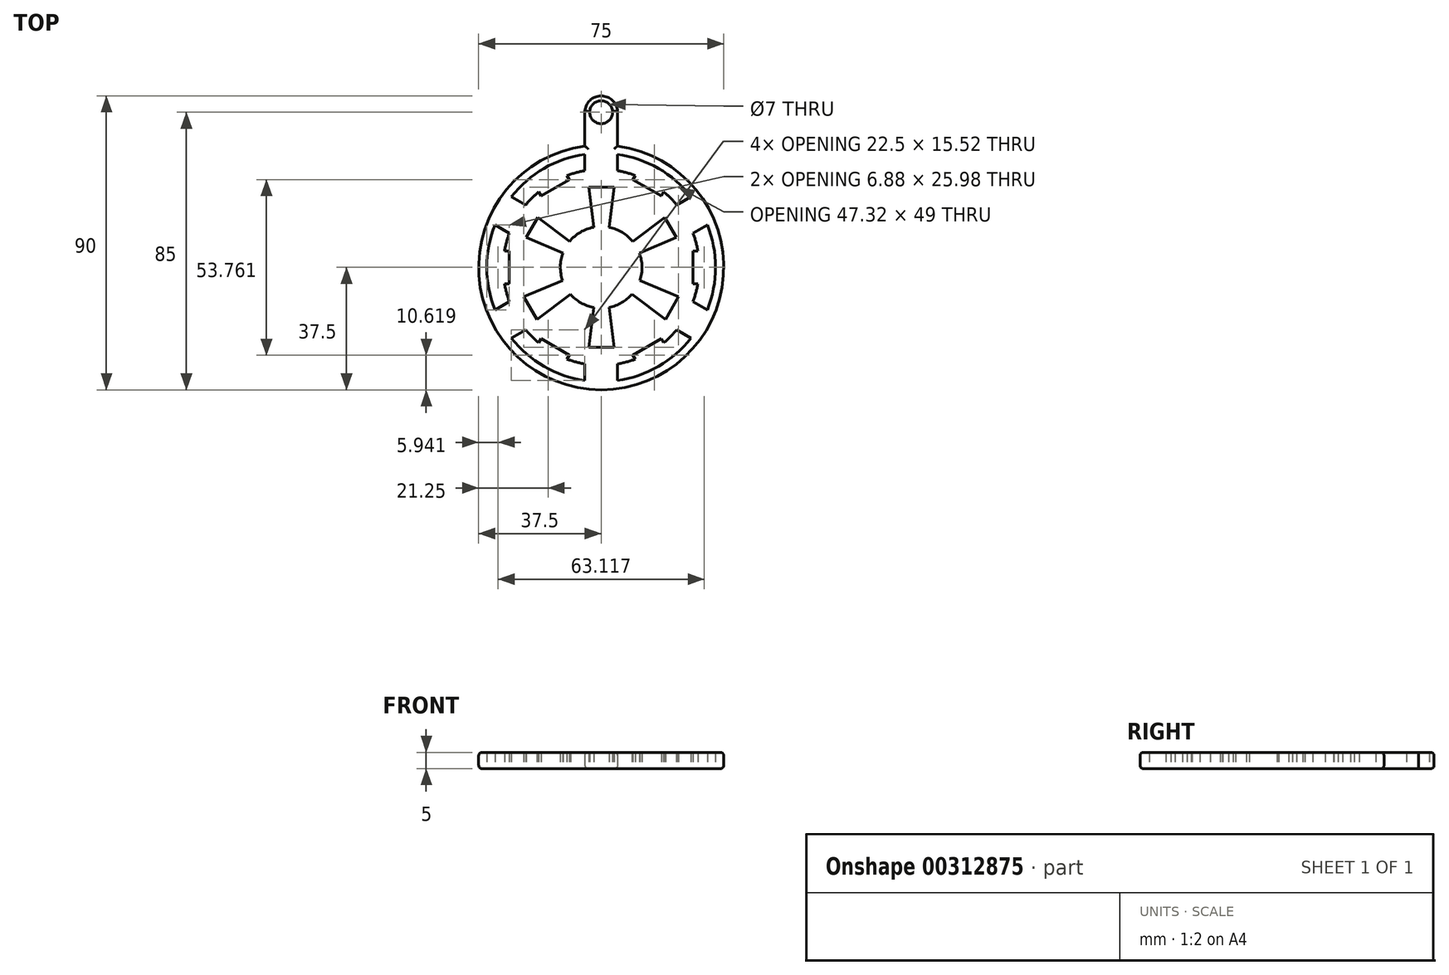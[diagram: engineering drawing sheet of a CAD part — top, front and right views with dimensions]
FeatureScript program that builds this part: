
annotation { "Feature Type Name" : "Feature", "Feature Type Description" : "" }
export const myFeature = defineFeature(function(context is Context, id is Id, definition is map)
    precondition{}
    {
        {
            var Q0;
            Q0=qCreatedBy(makeId("Top.planeOp"),FACE);
            var sketch = newSketch(context, id + "F0", { "sketchPlane" : qUnion([Q0])});
            skArc(sketch, "E0", {"start": v(-5, 29.58) * mm, "mid": v(-7.76, 28.98) * mm, "end": v(-10.46, 28.12) * mm});
            skLineSegment(sketch, "E1", {"start": v(-5, 30) * mm, "end": v(-5, 34.64) * mm});
            skLineSegment(sketch, "E2", {"start": v(5, 30) * mm, "end": v(5, 34.64) * mm});
            skLineSegment(sketch, "E3", {"start": v(-5, 30) * mm, "end": v(-5, 29.58) * mm});
            skLineSegment(sketch, "E4", {"start": v(5, 30) * mm, "end": v(5, 29.58) * mm});
            skLineSegment(sketch, "E5", {"start": v(-5, -30) * mm, "end": v(-5, -34.64) * mm});
            skLineSegment(sketch, "E6", {"start": v(-5, -30) * mm, "end": v(-5, -29.58) * mm});
            skArc(sketch, "E7.trimOffspring", {"start": v(5, -29.58) * mm, "mid": v(7.76, -28.98) * mm, "end": v(10.46, -28.12) * mm});
            skLineSegment(sketch, "E8.MirrorCS", {"start": v(5, -30) * mm, "end": v(5, -29.58) * mm});
            skLineSegment(sketch, "E9.MirrorCS", {"start": v(5, -30) * mm, "end": v(5, -34.64) * mm});
            skLineSegment(sketch, "E10", {"start": v(-27.5, 21.65) * mm, "end": v(-23.12, 19.12) * mm});
            skLineSegment(sketch, "E11", {"start": v(-32.5, 13) * mm, "end": v(-28.12, 10.46) * mm});
            skArc(sketch, "E12.trimOffspring", {"start": v(-28.12, 10.46) * mm, "mid": v(-28.98, 7.76) * mm, "end": v(-29.58, 5) * mm});
            skLineSegment(sketch, "E13", {"start": v(-27.5, -21.65) * mm, "end": v(-23.12, -19.12) * mm});
            skLineSegment(sketch, "E14", {"start": v(-32.5, -13) * mm, "end": v(-28.12, -10.46) * mm});
            skArc(sketch, "E15.trimOffspring", {"start": v(-23.12, -19.12) * mm, "mid": v(-21.21, -21.21) * mm, "end": v(-19.12, -23.12) * mm});
            skLineSegment(sketch, "E16.MirrorCS", {"start": v(27.5, 21.65) * mm, "end": v(23.12, 19.12) * mm});
            skLineSegment(sketch, "E17.MirrorCS", {"start": v(32.5, 13) * mm, "end": v(28.12, 10.46) * mm});
            skLineSegment(sketch, "E18.MirrorCS", {"start": v(32.5, -13) * mm, "end": v(28.12, -10.46) * mm});
            skLineSegment(sketch, "E19.MirrorCS", {"start": v(27.5, -21.65) * mm, "end": v(23.12, -19.12) * mm});
            skArc(sketch, "E20.trimOffspring", {"start": v(23.12, 19.12) * mm, "mid": v(21.21, 21.21) * mm, "end": v(19.12, 23.12) * mm});
            skArc(sketch, "E21.trimOffspring", {"start": v(28.12, -10.46) * mm, "mid": v(28.98, -7.76) * mm, "end": v(29.58, -5) * mm});
            skCircle(sketch, "E22", {"center": v(0, 0) * mm, "radius": 37.5 * mm});
            skLineSegment(sketch, "E23", {"start": v(-18.39, 21.85) * mm, "end": v(-9.73, 26.85) * mm});
            skLineSegment(sketch, "E24", {"start": v(-9.73, 26.85) * mm, "end": v(-10.46, 28.12) * mm});
            skLineSegment(sketch, "E25", {"start": v(-18.39, 21.85) * mm, "end": v(-19.12, 23.12) * mm});
            skArc(sketch, "E26.trimOffspring", {"start": v(-19.12, 23.12) * mm, "mid": v(-21.21, 21.21) * mm, "end": v(-23.12, 19.12) * mm});
            skPoint(sketch, "E27.start.orphan", {"position": v(-14.06, 24.35) * mm});
            skLineSegment(sketch, "E28", {"start": v(-28.12, 5) * mm, "end": v(-28.12, -5) * mm});
            skPoint(sketch, "E29.endSnap0", {"position": v(-28.12, 0) * mm});
            skLineSegment(sketch, "E30", {"start": v(-28.12, 5) * mm, "end": v(-29.58, 5) * mm});
            skLineSegment(sketch, "E31", {"start": v(-28.12, -5) * mm, "end": v(-29.58, -5) * mm});
            skArc(sketch, "E32.trimOffspring", {"start": v(-29.58, -5) * mm, "mid": v(-28.98, -7.76) * mm, "end": v(-28.12, -10.46) * mm});
            skPoint(sketch, "E29.start.orphan", {"position": v(-28.12, 0) * mm});
            skLineSegment(sketch, "E33", {"start": v(-9.73, -26.85) * mm, "end": v(-18.39, -21.85) * mm});
            skLineSegment(sketch, "E34", {"start": v(-9.73, -26.85) * mm, "end": v(-10.46, -28.12) * mm});
            skLineSegment(sketch, "E35", {"start": v(-18.39, -21.85) * mm, "end": v(-19.12, -23.12) * mm});
            skArc(sketch, "E36.trimOffspring", {"start": v(-10.46, -28.12) * mm, "mid": v(-7.76, -28.98) * mm, "end": v(-5, -29.58) * mm});
            skPoint(sketch, "E37.start.orphan", {"position": v(-14.06, -24.35) * mm});
            skLineSegment(sketch, "E38.MirrorCS", {"start": v(18.39, 21.85) * mm, "end": v(9.73, 26.85) * mm});
            skLineSegment(sketch, "E39.MirrorCS", {"start": v(9.73, 26.85) * mm, "end": v(10.46, 28.12) * mm});
            skLineSegment(sketch, "E40.MirrorCS", {"start": v(18.39, 21.85) * mm, "end": v(19.12, 23.12) * mm});
            skLineSegment(sketch, "E41.MirrorCS", {"start": v(28.12, 5) * mm, "end": v(29.58, 5) * mm});
            skLineSegment(sketch, "E42.MirrorCS", {"start": v(28.12, 5) * mm, "end": v(28.12, -5) * mm});
            skLineSegment(sketch, "E43.MirrorCS", {"start": v(28.12, -5) * mm, "end": v(29.58, -5) * mm});
            skLineSegment(sketch, "E44.MirrorCS", {"start": v(9.73, -26.85) * mm, "end": v(18.39, -21.85) * mm});
            skLineSegment(sketch, "E45.MirrorCS", {"start": v(9.73, -26.85) * mm, "end": v(10.46, -28.12) * mm});
            skLineSegment(sketch, "E46.MirrorCS", {"start": v(18.39, -21.85) * mm, "end": v(19.12, -23.12) * mm});
            skArc(sketch, "E47.trimOffspring", {"start": v(19.12, -23.12) * mm, "mid": v(21.21, -21.21) * mm, "end": v(23.12, -19.12) * mm});
            skArc(sketch, "E48.trimOffspring", {"start": v(29.58, 5) * mm, "mid": v(28.98, 7.76) * mm, "end": v(28.12, 10.46) * mm});
            skArc(sketch, "E49.trimOffspring", {"start": v(10.46, 28.12) * mm, "mid": v(7.76, 28.98) * mm, "end": v(5, 29.58) * mm});
            skArc(sketch, "E50", {"start": v(-2.32, 12.28) * mm, "mid": v(-6.37, 10.75) * mm, "end": v(-9.67, 7.93) * mm});
            skLineSegment(sketch, "E51", {"start": v(-2.32, 12.28) * mm, "end": v(-3.82, 24.5) * mm});
            skLineSegment(sketch, "E52", {"start": v(2.5, 12.25) * mm, "end": v(4, 24.5) * mm});
            skLineSegment(sketch, "E53", {"start": v(4, 24.5) * mm, "end": v(-3.82, 24.5) * mm});
            skLineSegment(sketch, "E54", {"start": v(-11.7, 4.4) * mm, "end": v(-22.98, 9.2) * mm});
            skLineSegment(sketch, "E55.MirrorCS", {"start": v(-9.67, 7.93) * mm, "end": v(-19.45, 15.3) * mm});
            skPoint(sketch, "E56.start.orphan", {"position": v(-22.23, 10.5) * mm});
            skPoint(sketch, "E57.start.orphan", {"position": v(-10.83, 6.25) * mm});
            skPoint(sketch, "E58.MirrorCS.end.orphan", {"position": v(-9.81, 8) * mm});
            skPoint(sketch, "E59.start.orphan", {"position": v(-11.84, 4.5) * mm});
            skArc(sketch, "E60.trimOffspring", {"start": v(-11.7, 4.4) * mm, "mid": v(-12.5, 0.2) * mm, "end": v(-11.83, -4.04) * mm});
            skPoint(sketch, "E61.MirrorCS.end.orphan", {"position": v(-19.45, 15.3) * mm});
            skPoint(sketch, "E61.MirrorCS.start.orphan", {"position": v(-20.2, 14) * mm});
            skLineSegment(sketch, "E62", {"start": v(-22.98, 9.2) * mm, "end": v(-19.45, 15.3) * mm});
            skLineSegment(sketch, "E63.MirrorCS", {"start": v(9.67, 7.93) * mm, "end": v(19.45, 15.3) * mm});
            skLineSegment(sketch, "E64.MirrorCS", {"start": v(11.7, 4.4) * mm, "end": v(22.98, 9.2) * mm});
            skLineSegment(sketch, "E65.MirrorCS", {"start": v(22.98, 9.2) * mm, "end": v(19.45, 15.3) * mm});
            skArc(sketch, "E66.trimOffspring", {"start": v(9.67, 7.93) * mm, "mid": v(6.46, 10.7) * mm, "end": v(2.5, 12.25) * mm});
            skLineSegment(sketch, "E67.MirrorCS", {"start": v(-2.32, -12.28) * mm, "end": v(-3.82, -24.5) * mm});
            skLineSegment(sketch, "E68.MirrorCS", {"start": v(2.5, -12.25) * mm, "end": v(4, -24.5) * mm});
            skLineSegment(sketch, "E69.MirrorCS", {"start": v(4, -24.5) * mm, "end": v(-3.82, -24.5) * mm});
            skArc(sketch, "E70.trimOffspring", {"start": v(2.5, -12.25) * mm, "mid": v(10.94, -6.04) * mm, "end": v(11.7, 4.4) * mm});
            skLineSegment(sketch, "E71", {"start": v(-23.66, -9.04) * mm, "end": v(-11.83, -4.04) * mm});
            skLineSegment(sketch, "E72.MirrorCS", {"start": v(-19.66, -15.97) * mm, "end": v(-9.42, -8.22) * mm});
            skPoint(sketch, "E73.start.orphan", {"position": v(-11.27, -6.5) * mm});
            skPoint(sketch, "E74.MirrorCS.end.orphan", {"position": v(-10.02, -8.67) * mm});
            skPoint(sketch, "E75.start.orphan", {"position": v(-12.52, -4.34) * mm});
            skPoint(sketch, "E76.start.orphan", {"position": v(-22.9, -10.34) * mm});
            skPoint(sketch, "E77.MirrorCS.end.orphan", {"position": v(-20.4, -14.67) * mm});
            skPoint(sketch, "E78.MirrorCS.end.orphan", {"position": v(-19.66, -15.97) * mm});
            skLineSegment(sketch, "E79", {"start": v(-19.66, -15.97) * mm, "end": v(-23.66, -9.04) * mm});
            skArc(sketch, "E80.trimOffspring", {"start": v(-9.42, -8.22) * mm, "mid": v(-6.2, -10.85) * mm, "end": v(-2.32, -12.28) * mm});
            skLineSegment(sketch, "E81.MirrorCS", {"start": v(23.66, -9.04) * mm, "end": v(11.83, -4.04) * mm});
            skLineSegment(sketch, "E82.MirrorCS", {"start": v(19.66, -15.97) * mm, "end": v(9.42, -8.22) * mm});
            skLineSegment(sketch, "E83.MirrorCS", {"start": v(19.66, -15.97) * mm, "end": v(23.66, -9.04) * mm});
            skArc(sketch, "E84", {"start": v(-32.5, 13) * mm, "mid": v(-35, 0) * mm, "end": v(-32.5, -13) * mm});
            skArc(sketch, "E85.trimOffspring", {"start": v(-27.5, -21.65) * mm, "mid": v(-17.5, -30.31) * mm, "end": v(-5, -34.64) * mm});
            skArc(sketch, "E86.trimOffspring", {"start": v(5, -34.64) * mm, "mid": v(17.5, -30.31) * mm, "end": v(27.5, -21.65) * mm});
            skArc(sketch, "E87.trimOffspring", {"start": v(32.5, -13) * mm, "mid": v(35, 0) * mm, "end": v(32.5, 13) * mm});
            skArc(sketch, "E88.trimOffspring", {"start": v(27.5, 21.65) * mm, "mid": v(17.5, 30.31) * mm, "end": v(5, 34.64) * mm});
            skArc(sketch, "E89.trimOffspring", {"start": v(-5, 34.64) * mm, "mid": v(-17.5, 30.31) * mm, "end": v(-27.5, 21.65) * mm});
            skCircle(sketch, "E90", {"center": v(0, 47.5) * mm, "radius": 5 * mm});
            skLineSegment(sketch, "E91", {"start": v(-4.99, 47.77) * mm, "end": v(-4.99, 37.17) * mm});
            skLineSegment(sketch, "E92.MirrorCS", {"start": v(4.99, 47.77) * mm, "end": v(4.99, 37.17) * mm});
            skCircle(sketch, "E93", {"center": v(0, 47.5) * mm, "radius": 3.5 * mm});
            skSolve(sketch);
        }
        {
            var Q0;
            Q0=makeQuery(id+"F0.imprint","IMPRINT",FACE,{"disambiguationData":[TD([[makeQuery(id+"F0.imprint","IMPRINT",EDGE,{"derivedFrom":sQuery(id+"F0.wireOp",EDGE,"E0")}),1.0]])]});
            extrude(context, id + "F1", {"entities" : qUnion([Q0]), "depth" : 5 * mm});
        }
        {
            var Q0;
            {var subQ0=sQuery(id+"F0.wireOp",EDGE,"E91");var subQ1=sQuery(id+"F0.wireOp",EDGE,"E22");var subQ2=makeQuery(id+"F0.imprint","INTERSECT",VERTEX,{"derivedFrom":[subQ1,subQ0]});Q0=makeQuery(id+"F0.imprint","IMPRINT",FACE,{"disambiguationData":[TD([[makeQuery(id+"F0.imprint","IMPRINT",EDGE,{"disambiguationData":[TD([[subQ2,1.0]])],"derivedFrom":subQ1}),-1.0]])]});}
            var Q1;
            Q1=makeQuery(id+"F0.imprint","IMPRINT",FACE,{"disambiguationData":[TD([[makeQuery(id+"F0.imprint","IMPRINT",EDGE,{"derivedFrom":sQuery(id+"F0.wireOp",EDGE,"E93")}),-1.0]])]});
            extrude(context, id + "F2", {"entities" : qUnion([Q0, Q1]), "operationType" : NewBodyOperationType.ADD, "depth" : 5 * mm});
        }
        {
            var Q0;
            Q0=makeQuery(id+"F2.opExtrude","CAP_EDGE",EDGE,{"disambiguationData":[OSD([sQuery(id+"F0.wireOp",EDGE,"E92.MirrorCS")])],"isStart":true});
            var Q1;
            Q1=makeQuery(id+"F2.opExtrude","CAP_EDGE",EDGE,{"disambiguationData":[OSD([sQuery(id+"F0.wireOp",EDGE,"E91")])],"isStart":true});
            var Q2;
            Q2=makeQuery(id+"F2.opExtrude","CAP_EDGE",EDGE,{"disambiguationData":[OSD([sQuery(id+"F0.wireOp",EDGE,"E92.MirrorCS")])],"isStart":false});
            var Q3;
            Q3=makeQuery(id+"F2.opExtrude","CAP_EDGE",EDGE,{"disambiguationData":[OSD([sQuery(id+"F0.wireOp",EDGE,"E91")])],"isStart":false});
            var Q4;
            Q4=makeQuery(id+"F2.opExtrude","CAP_EDGE",EDGE,{"disambiguationData":[OSD([sQuery(id+"F0.wireOp",EDGE,"E90")])],"isStart":false});
            var Q5;
            Q5=makeQuery(id+"F2.opExtrude","CAP_EDGE",EDGE,{"disambiguationData":[OSD([sQuery(id+"F0.wireOp",EDGE,"E90")])],"isStart":true});
            var Q6;
            Q6=makeQuery(id+"F1.opExtrude","CAP_EDGE",EDGE,{"disambiguationData":[OSD([sQuery(id+"F0.wireOp",EDGE,"E22")])],"isStart":true});
            var Q7;
            Q7=makeQuery(id+"F1.opExtrude","CAP_EDGE",EDGE,{"disambiguationData":[OSD([sQuery(id+"F0.wireOp",EDGE,"E22")])],"isStart":false});
            fillet(context, id + "F3", {"entities" : qUnion([Q0, Q1, Q2, Q3, Q4, Q5, Q6, Q7]), "radius" : 1 * mm, "tangentPropagation" : true, "allowEdgeOverflow" : false});
        }
    });
